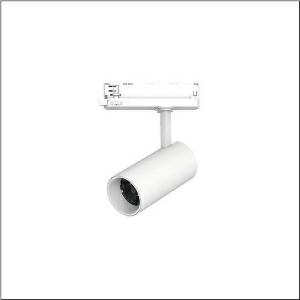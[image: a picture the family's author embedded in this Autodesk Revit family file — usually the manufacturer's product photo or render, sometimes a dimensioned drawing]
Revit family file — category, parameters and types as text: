
# Revit family: spot_31_slim_51sf127fa1b
name_source: partatom
category: Lighting Fixtures
units: mm (PartAtom-declared; Revit-internal decimal feet)

## family parameters
Cut with Voids When Loaded = No
Host = Face
Light Source = No
Part Type = Normal
Room Calculation Point = No
Round Connector Dimension = Use Diameter
Shared = No

## types (1)
- Spot 31 Slim (1 x LED, 2090 lm, 16.3 W, 2700K)
    Apparent Load = 16 VA
    CIE Flux Codes = 94 98 99 100 100
    Color Rendering = 90
    Color Temperature = 2700K
    Default Elevation = 1800 mm
    Description = Spot 31 Slim, directional spotlight, light control with reflector, of aluminium, LED rated luminous flux: 2.100lm, light colour: 927, control gear: ECG, with 3-phase adapter, mains connection: 220..240V, AC, 50/60Hz, housing, of aluminium, traffic white (RAL 9016), diameter: 70mm, adapter, of plastic, protection rating (complete): IP20, insulation class (complete): insulation class I (protective earthing), certification: CE, impact resistance: IK02, packaging unit: 1 piece
    Height = 210 mm
    Lamp = 1 x LED
    Lamp Light Flux = 2090 lm
    Lamp Power = 16.3 W
    Lamp count = 1
    Length = 70 mm
    Luminous efficacy = 128 lm/W
    Manufacturer = Siteco
    ModVariant = No
    Model = 51SF127FA1B
    Mounting Place = Ceiling
    Mounting Type = Pendant
    Number of Poles = 1
    OnlyDefault = Yes
    Power Factor = 1
    Product Name = Spot 31 Slim
    Product group = directional spotlight
    ProductGroupID = 906
    Protection Class = Protection class I
    Protection Degree = IP 20
    RLX_Detail_Level = 1
    RLX_Emergency_Light_Flux = 0 lm
    RLX_Emergency_Type = 0
    RLX_Emergency_Type_DB = No
    RlxData = <blob elided: 13505 chars, md5=96f67cf0>
    Socket = socket
    Standby Power = 0 W
    System Light Flux = 2090 lm
    System Power = 16 W
    Type Comments = Product without accessories
    Type Image = l_1228470.jpg
    URL = http://relux.com
    VarID = ---
    Voltage = 0 V
    Weight = 0.00 kg
    Width = 0 mm  [stored 0 ft]

note: [stored X ft] marks values corroborated as IEEE doubles in the binary element streams (Revit-internal decimal feet)

## geometry (parser evidence)
native form markers: Sweep x9
no freeform markers — native parametric forms only
